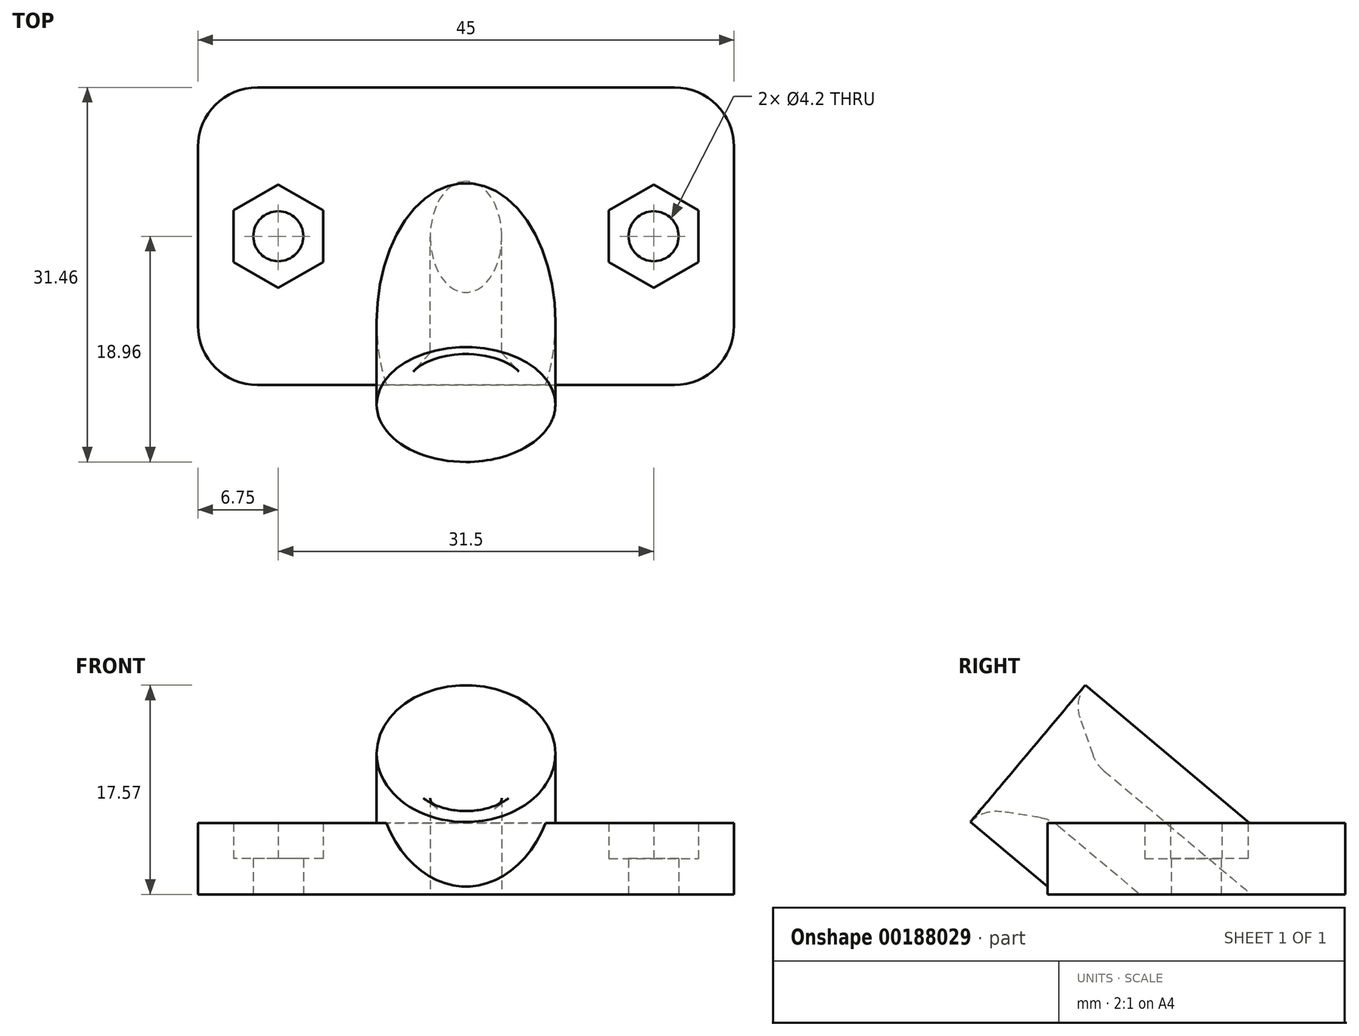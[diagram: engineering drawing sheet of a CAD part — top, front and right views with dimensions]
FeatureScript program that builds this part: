
annotation { "Feature Type Name" : "Feature", "Feature Type Description" : "" }
export const myFeature = defineFeature(function(context is Context, id is Id, definition is map)
    precondition{}
    {
        {
            var Q0;
            Q0=qCreatedBy(makeId("Top.planeOp"),FACE);
            var sketch = newSketch(context, id + "F0", { "sketchPlane" : qUnion([Q0])});
            skLineSegment(sketch, "E0.bottom", {"start": v(0, 0) * mm, "end": v(45, 0) * mm});
            skLineSegment(sketch, "E0.top", {"start": v(0, 25) * mm, "end": v(45, 25) * mm});
            skLineSegment(sketch, "E0.left", {"start": v(0, 0) * mm, "end": v(0, 25) * mm});
            skLineSegment(sketch, "E0.right", {"start": v(45, 0) * mm, "end": v(45, 25) * mm});
            skSolve(sketch);
        }
        {
            var Q0;
            Q0=makeQuery(id+"F0.imprint","IMPRINT",FACE,{"disambiguationData":[TD([[makeQuery(id+"F0.imprint","IMPRINT",EDGE,{"derivedFrom":sQuery(id+"F0.wireOp",EDGE,"E0.bottom")}),1.0]])]});
            extrude(context, id + "F1", {"entities" : qUnion([Q0]), "depth" : 6 * mm});
        }
        {
            var Q0;
            Q0=makeQuery(id+"F1.opExtrude","SWEPT_EDGE",EDGE,{"disambiguationData":[OSD([sQuery(id+"F0.wireOp",EDGE,"E0.top"),sQuery(id+"F0.wireOp",EDGE,"E0.right")])]});
            var Q1;
            Q1=makeQuery(id+"F1.opExtrude","SWEPT_EDGE",EDGE,{"disambiguationData":[OSD([sQuery(id+"F0.wireOp",EDGE,"E0.bottom"),sQuery(id+"F0.wireOp",EDGE,"E0.right")])]});
            var Q2;
            Q2=makeQuery(id+"F1.opExtrude","SWEPT_EDGE",EDGE,{"disambiguationData":[OSD([sQuery(id+"F0.wireOp",EDGE,"E0.top"),sQuery(id+"F0.wireOp",EDGE,"E0.left")])]});
            var Q3;
            Q3=makeQuery(id+"F1.opExtrude","SWEPT_EDGE",EDGE,{"disambiguationData":[OSD([sQuery(id+"F0.wireOp",EDGE,"E0.bottom"),sQuery(id+"F0.wireOp",EDGE,"E0.left")])]});
            fillet(context, id + "F2", {"entities" : qUnion([Q0, Q1, Q2, Q3]), "radius" : 5 * mm, "tangentPropagation" : true, "allowEdgeOverflow" : false});
        }
        {
            var Q0;
            Q0=qCreatedBy(makeId("Top.planeOp"),FACE);
            cPlane(context, id + "F3", {"entities" : qUnion([Q0]), "cplaneType" : CPlaneType.OFFSET, "offset" : 3 * mm, "width" : 150 * mm, "height" : 150 * mm});
        }
        {
            var Q0;
            Q0=qCreatedBy(id+"F3.planeOp",FACE);
            var sketch = newSketch(context, id + "F4", { "sketchPlane" : qUnion([Q0])});
            skCircle(sketch, "E1.cCircle", {"center": v(6.75, 12.5) * mm, "radius": 3.75 * mm, "construction": true});
            skLineSegment(sketch, "E1.0", {"start": v(3, 10.33) * mm, "end": v(3, 14.67) * mm});
            skLineSegment(sketch, "E1.1", {"start": v(3, 14.67) * mm, "end": v(6.75, 16.83) * mm});
            skLineSegment(sketch, "E1.2", {"start": v(6.75, 16.83) * mm, "end": v(10.5, 14.67) * mm});
            skLineSegment(sketch, "E1.3", {"start": v(10.5, 14.67) * mm, "end": v(10.5, 10.33) * mm});
            skLineSegment(sketch, "E1.4", {"start": v(10.5, 10.33) * mm, "end": v(6.75, 8.17) * mm});
            skLineSegment(sketch, "E1.5", {"start": v(6.75, 8.17) * mm, "end": v(3, 10.33) * mm});
            skPoint(sketch, "E1.0.midPoint", {"position": v(3, 12.5) * mm});
            skCircle(sketch, "E2.cCircle", {"center": v(38.25, 12.5) * mm, "radius": 3.75 * mm, "construction": true});
            skLineSegment(sketch, "E2.0", {"start": v(42, 14.67) * mm, "end": v(42, 10.33) * mm});
            skLineSegment(sketch, "E2.1", {"start": v(42, 10.33) * mm, "end": v(38.25, 8.17) * mm});
            skLineSegment(sketch, "E2.2", {"start": v(38.25, 8.17) * mm, "end": v(34.5, 10.33) * mm});
            skLineSegment(sketch, "E2.3", {"start": v(34.5, 10.33) * mm, "end": v(34.5, 14.67) * mm});
            skLineSegment(sketch, "E2.4", {"start": v(34.5, 14.67) * mm, "end": v(38.25, 16.83) * mm});
            skLineSegment(sketch, "E2.5", {"start": v(38.25, 16.83) * mm, "end": v(42, 14.67) * mm});
            skPoint(sketch, "E2.0.midPoint", {"position": v(42, 12.5) * mm});
            skSolve(sketch);
        }
        {
            var Q0;
            Q0 = qSketchRegion(id + "F4", true);
            extrude(context, id + "F5", {"entities" : qUnion([Q0]), "operationType" : NewBodyOperationType.REMOVE, "depth" : 25 * mm});
        }
        {
            var Q0;
            Q0=qCreatedBy(makeId("Top.planeOp"),FACE);
            var sketch = newSketch(context, id + "F6", { "sketchPlane" : qUnion([Q0])});
            skCircle(sketch, "E3", {"center": v(6.75, 12.5) * mm, "radius": 2.1 * mm});
            skCircle(sketch, "E4", {"center": v(38.25, 12.5) * mm, "radius": 2.1 * mm});
            skSolve(sketch);
        }
        {
            var Q0;
            Q0 = qSketchRegion(id + "F6", true);
            extrude(context, id + "F7", {"entities" : qUnion([Q0]), "operationType" : NewBodyOperationType.REMOVE, "depth" : 25 * mm});
        }
        {
            var Q0;
            Q0=makeQuery(id+"F1.opExtrude","CAP_EDGE",EDGE,{"disambiguationData":[OSD([sQuery(id+"F0.wireOp",EDGE,"E0.bottom")])],"isStart":false});
            cPlane(context, id + "F8", {"entities" : qUnion([Q0]), "cplaneType" : CPlaneType.LINE_ANGLE, "offset" : 25 * mm, "angle" : 140 * degree, "width" : 150 * mm, "height" : 150 * mm});
        }
        {
            var Q0;
            Q0=qCreatedBy(id+"F8.planeOp",FACE);
            var sketch = newSketch(context, id + "F9", { "sketchPlane" : qUnion([Q0])});
            skCircle(sketch, "E5", {"center": v(22.5, 8) * mm, "radius": 7.5 * mm});
            skSolve(sketch);
        }
        {
            var Q0;
            Q0 = qSketchRegion(id + "F9", true);
            extrude(context, id + "F10", {"entities" : qUnion([Q0]), "operationType" : NewBodyOperationType.ADD, "depth" : 5 * mm, "hasSecondDirection" : true, "secondDirectionOppositeDirection" : true, "secondDirectionDepth" : 25 * mm});
        }
        {
            var Q0;
            Q0=qCreatedBy(makeId("Top.planeOp"),FACE);
            var sketch = newSketch(context, id + "F11", { "sketchPlane" : qUnion([Q0])});
            skLineSegment(sketch, "E6.bottom", {"start": v(-1.96, -1.35) * mm, "end": v(47.32, -1.35) * mm});
            skLineSegment(sketch, "E6.top", {"start": v(-1.96, 28.88) * mm, "end": v(47.32, 28.88) * mm});
            skLineSegment(sketch, "E6.left", {"start": v(-1.96, -1.35) * mm, "end": v(-1.96, 28.88) * mm});
            skLineSegment(sketch, "E6.right", {"start": v(47.32, -1.35) * mm, "end": v(47.32, 28.88) * mm});
            skSolve(sketch);
        }
        {
            var Q0;
            Q0 = qSketchRegion(id + "F11", true);
            extrude(context, id + "F12", {"entities" : qUnion([Q0]), "operationType" : NewBodyOperationType.REMOVE, "oppositeDirection" : true, "depth" : 25 * mm});
        }
        {
            var Q0;
            Q0=makeQuery(id+"F1.opExtrude","SWEPT_FACE",FACE,{"disambiguationData":[OSD([sQuery(id+"F0.wireOp",EDGE,"E0.top")])]});
            var sketch = newSketch(context, id + "F13", { "sketchPlane" : qUnion([Q0])});
            skLineSegment(sketch, "E7.bottom", {"start": v(-3.87, 7.72) * mm, "end": v(-41.53, 7.72) * mm});
            skLineSegment(sketch, "E7.top", {"start": v(-3.87, -2.98) * mm, "end": v(-41.53, -2.98) * mm});
            skLineSegment(sketch, "E7.left", {"start": v(-3.87, 7.72) * mm, "end": v(-3.87, -2.98) * mm});
            skLineSegment(sketch, "E7.right", {"start": v(-41.53, 7.72) * mm, "end": v(-41.53, -2.98) * mm});
            skSolve(sketch);
        }
        {
            var Q0;
            Q0 = qSketchRegion(id + "F13", true);
            extrude(context, id + "F14", {"entities" : qUnion([Q0]), "operationType" : NewBodyOperationType.REMOVE, "depth" : 25 * mm});
        }
        {
            var Q0;
            Q0=qCreatedBy(id+"F8.planeOp",FACE);
            var sketch = newSketch(context, id + "F15", { "sketchPlane" : qUnion([Q0])});
            skCircle(sketch, "E8", {"center": v(22.5, 8) * mm, "radius": 3 * mm});
            skSolve(sketch);
        }
        {
            var Q0;
            Q0 = qSketchRegion(id + "F15", true);
            extrude(context, id + "F16", {"entities" : qUnion([Q0]), "operationType" : NewBodyOperationType.REMOVE, "depth" : 25 * mm, "hasSecondDirection" : true, "secondDirectionOppositeDirection" : true, "secondDirectionDepth" : 25 * mm});
        }
        {
            var Q0;
            Q0=makeQuery(id+"F16.boolean.opBoolean","INTERSECT",EDGE,{"derivedFrom":[makeQuery(id+"F10.opExtrude","CAP_FACE",FACE,{"disambiguationData":[OSD([sQuery(id+"F9.wireOp",EDGE,"E5")])],"isStart":false}),makeQuery(id+"F16.opExtrude","SWEPT_FACE",FACE,{"disambiguationData":[OSD([sQuery(id+"F15.wireOp",EDGE,"E8")])]})]});
            chamfer(context, id + "F17", {"entities" : qUnion([Q0]), "chamferType" : ChamferType.TWO_OFFSETS, "width1" : 3 * mm, "oppositeDirection" : false, "width2" : 5 * mm, "tangentPropagation" : true});
        }
        {
            var Q0;
            {var subQ0=makeQuery(id+"F16.opExtrude","SWEPT_FACE",FACE,{"disambiguationData":[OSD([sQuery(id+"F15.wireOp",EDGE,"E8")])]});Q0=makeQuery(id+"F17.opChamfer","BLEND_EDGE",EDGE,{"blendedFrom":[makeQuery(id+"F16.boolean.opBoolean","INTERSECT",EDGE,{"derivedFrom":[makeQuery(id+"F10.opExtrude","CAP_FACE",FACE,{"disambiguationData":[OSD([sQuery(id+"F9.wireOp",EDGE,"E5")])],"isStart":false}),subQ0]}),makeQuery(id+"F16.boolean.opBoolean","COPY",FACE,{"derivedFrom":subQ0})],"blendedInto":[makeQuery(id+"F16.boolean.opBoolean","COPY",FACE,{"derivedFrom":subQ0})]});}
            fillet(context, id + "F18", {"entities" : qUnion([Q0]), "radius" : 3 * mm, "tangentPropagation" : true, "allowEdgeOverflow" : false});
        }
        {
            var Q0;
            {var subQ0=makeQuery(id+"F10.opExtrude","CAP_FACE",FACE,{"disambiguationData":[OSD([sQuery(id+"F9.wireOp",EDGE,"E5")])],"isStart":false});Q0=makeQuery(id+"F17.opChamfer","BLEND_EDGE",EDGE,{"blendedFrom":[makeQuery(id+"F16.boolean.opBoolean","INTERSECT",EDGE,{"derivedFrom":[subQ0,makeQuery(id+"F16.opExtrude","SWEPT_FACE",FACE,{"disambiguationData":[OSD([sQuery(id+"F15.wireOp",EDGE,"E8")])]})]}),subQ0],"blendedInto":[subQ0]});}
            fillet(context, id + "F19", {"entities" : qUnion([Q0]), "radius" : 3 * mm, "tangentPropagation" : true, "allowEdgeOverflow" : false});
        }
    });
